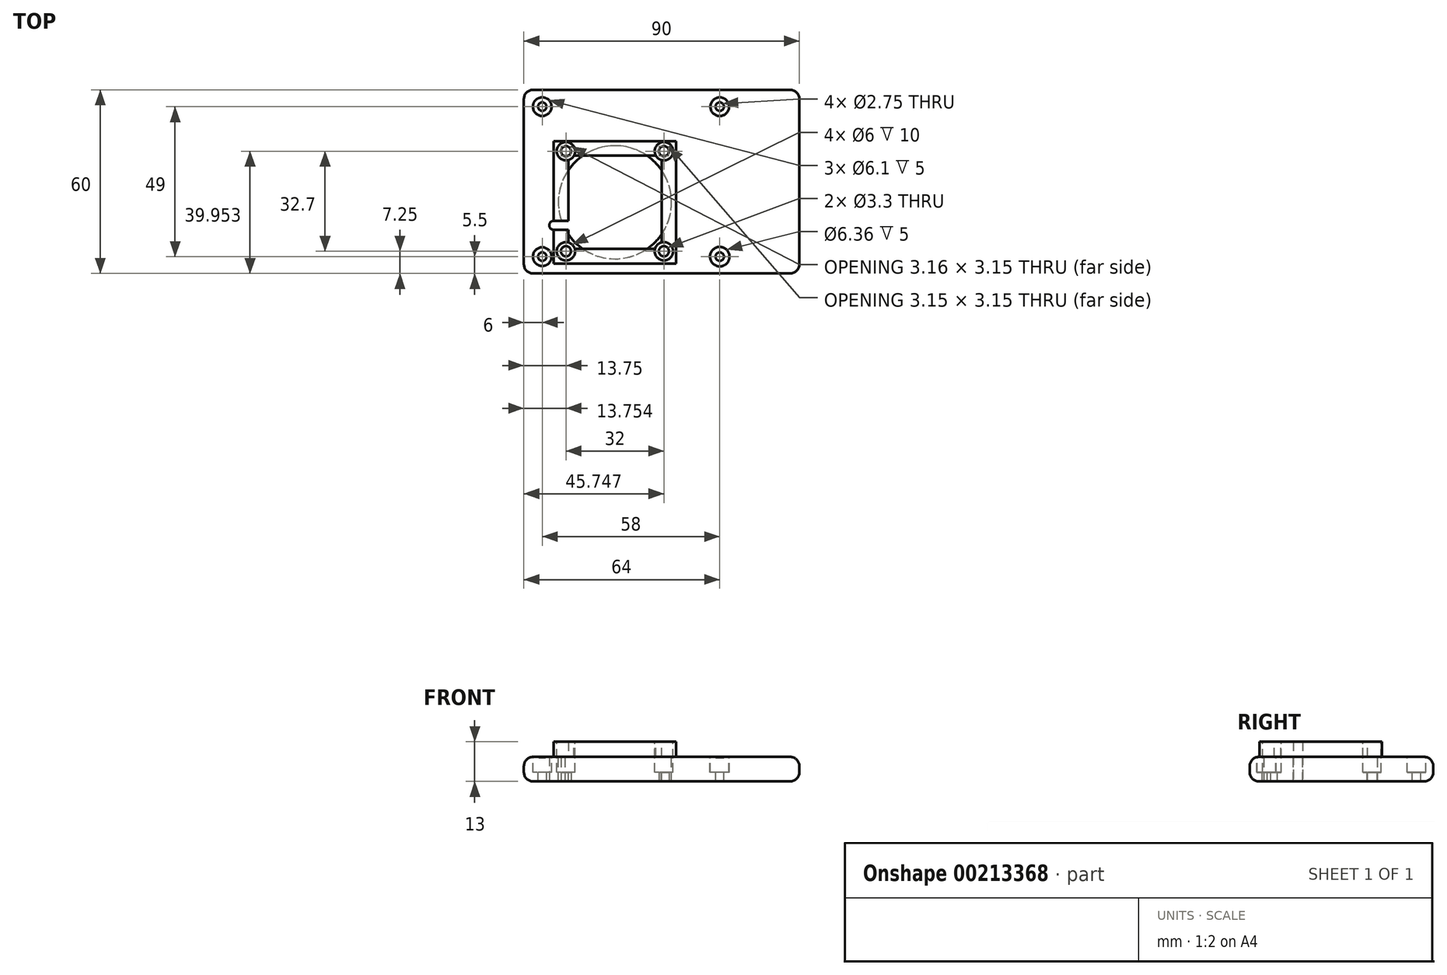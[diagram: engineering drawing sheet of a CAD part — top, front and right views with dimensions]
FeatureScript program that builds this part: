
annotation { "Feature Type Name" : "Feature", "Feature Type Description" : "" }
export const myFeature = defineFeature(function(context is Context, id is Id, definition is map)
    precondition{}
    {
        {
            var Q0;
            Q0=qCreatedBy(makeId("Top.planeOp"),FACE);
            var sketch = newSketch(context, id + "F0", { "sketchPlane" : qUnion([Q0])});
            skLineSegment(sketch, "E0.bottom", {"start": v(-45.78, -23.25) * mm, "end": v(38.22, -23.25) * mm});
            skLineSegment(sketch, "E0.top", {"start": v(-45.78, 36.75) * mm, "end": v(38.22, 36.75) * mm});
            skLineSegment(sketch, "E0.left", {"start": v(-48.78, -20.25) * mm, "end": v(-48.78, 33.75) * mm});
            skLineSegment(sketch, "E0.right", {"start": v(41.22, -20.25) * mm, "end": v(41.22, 33.75) * mm});
            skPoint(sketch, "E1.visualSharp", {"position": v(-48.78, 36.75) * mm});
            skArc(sketch, "E1.filletArc", {"start": v(-45.78, 36.75) * mm, "mid": v(-47.9, 35.87) * mm, "end": v(-48.78, 33.75) * mm});
            skPoint(sketch, "E2.visualSharp", {"position": v(41.22, 36.75) * mm});
            skArc(sketch, "E2.filletArc", {"start": v(41.22, 33.75) * mm, "mid": v(40.34, 35.87) * mm, "end": v(38.22, 36.75) * mm});
            skPoint(sketch, "E3.visualSharp", {"position": v(41.22, -23.25) * mm});
            skArc(sketch, "E3.filletArc", {"start": v(38.22, -23.25) * mm, "mid": v(40.34, -22.37) * mm, "end": v(41.22, -20.25) * mm});
            skPoint(sketch, "E4.visualSharp", {"position": v(-48.78, -23.25) * mm});
            skArc(sketch, "E4.filletArc", {"start": v(-48.78, -20.25) * mm, "mid": v(-47.9, -22.37) * mm, "end": v(-45.78, -23.25) * mm});
            skCircle(sketch, "E5", {"center": v(-42.78, -17.75) * mm, "radius": 1.38 * mm});
            skCircle(sketch, "E6", {"center": v(15.22, -17.75) * mm, "radius": 1.38 * mm});
            skCircle(sketch, "E7", {"center": v(-42.78, 31.25) * mm, "radius": 1.38 * mm});
            skCircle(sketch, "E8", {"center": v(15.22, 31.25) * mm, "radius": 1.38 * mm});
            skPoint(sketch, "E9", {"position": v(-29.78, 8.98) * mm});
            skPoint(sketch, "E10", {"position": v(2.22, -23.02) * mm});
            skLineSegment(sketch, "E11.bottom", {"start": v(-44.03, -20.25) * mm, "end": v(5.97, -20.25) * mm});
            skLineSegment(sketch, "E11.top", {"start": v(-44.03, 24.75) * mm, "end": v(5.97, 24.75) * mm});
            skLineSegment(sketch, "E11.left", {"start": v(-44.03, -20.25) * mm, "end": v(-44.03, 24.75) * mm});
            skLineSegment(sketch, "E11.right", {"start": v(5.97, -20.25) * mm, "end": v(5.97, 24.75) * mm});
            skLineSegment(sketch, "E12.bottom", {"start": v(-34.28, -15.25) * mm, "end": v(-3.78, -15.25) * mm});
            skLineSegment(sketch, "E12.top", {"start": v(-34.28, 15.25) * mm, "end": v(-3.78, 15.25) * mm});
            skLineSegment(sketch, "E12.left", {"start": v(-34.28, -15.25) * mm, "end": v(-34.28, 15.25) * mm});
            skLineSegment(sketch, "E12.right", {"start": v(-3.78, -15.25) * mm, "end": v(-3.78, 15.25) * mm});
            skCircle(sketch, "E13", {"center": v(-19.03, 0) * mm, "radius": 18.5 * mm});
            skLineSegment(sketch, "E14.bottom", {"start": v(0.97, 20) * mm, "end": v(-39.03, 20) * mm});
            skLineSegment(sketch, "E14.top", {"start": v(0.97, -20) * mm, "end": v(-39.03, -20) * mm});
            skLineSegment(sketch, "E14.left", {"start": v(0.97, 20) * mm, "end": v(0.97, -20) * mm});
            skLineSegment(sketch, "E14.right", {"start": v(-39.03, 20) * mm, "end": v(-39.03, -20) * mm});
            skCircle(sketch, "E15", {"center": v(-35.03, -16) * mm, "radius": 1.65 * mm});
            skCircle(sketch, "E16", {"center": v(-35.03, 16.7) * mm, "radius": 1.65 * mm});
            skCircle(sketch, "E17", {"center": v(-3.03, -16) * mm, "radius": 1.65 * mm});
            skCircle(sketch, "E18", {"center": v(-3.03, 16.7) * mm, "radius": 1.65 * mm});
            skCircle(sketch, "E19", {"center": v(15.22, 31.25) * mm, "radius": 3.05 * mm});
            skCircle(sketch, "E20", {"center": v(15.22, -17.75) * mm, "radius": 3.18 * mm});
            skCircle(sketch, "E21", {"center": v(-42.78, -17.75) * mm, "radius": 3.05 * mm});
            skCircle(sketch, "E22", {"center": v(-42.78, 31.25) * mm, "radius": 3.05 * mm});
            skSolve(sketch);
        }
        {
            var Q0;
            {var subQ0=sQuery(id+"F0.wireOp",EDGE,"E13");var subQ1=sQuery(id+"F0.wireOp",EDGE,"E12.bottom");var subQ2=makeQuery(id+"F0.imprint","INTERSECT",VERTEX,{"disambiguationData":[OD(0.0)],"derivedFrom":[subQ1,subQ0]});Q0=makeQuery(id+"F0.imprint","IMPRINT",FACE,{"disambiguationData":[TD([[makeQuery(id+"F0.imprint","IMPRINT",EDGE,{"disambiguationData":[TD([[subQ2,-1.0]])],"derivedFrom":subQ1}),-1.0]])]});}
            var Q1;
            {var subQ0=sQuery(id+"F0.wireOp",EDGE,"E13");var subQ1=sQuery(id+"F0.wireOp",EDGE,"E12.right");var subQ2=makeQuery(id+"F0.imprint","INTERSECT",VERTEX,{"disambiguationData":[OD(0.0)],"derivedFrom":[subQ1,subQ0]});Q1=makeQuery(id+"F0.imprint","IMPRINT",FACE,{"disambiguationData":[TD([[makeQuery(id+"F0.imprint","IMPRINT",EDGE,{"disambiguationData":[TD([[subQ2,-1.0]])],"derivedFrom":subQ1}),-1.0]])]});}
            var Q2;
            {var subQ0=sQuery(id+"F0.wireOp",EDGE,"E13");var subQ1=sQuery(id+"F0.wireOp",EDGE,"E12.top");var subQ2=makeQuery(id+"F0.imprint","INTERSECT",VERTEX,{"disambiguationData":[OD(0.0)],"derivedFrom":[subQ1,subQ0]});Q2=makeQuery(id+"F0.imprint","IMPRINT",FACE,{"disambiguationData":[TD([[makeQuery(id+"F0.imprint","IMPRINT",EDGE,{"disambiguationData":[TD([[subQ2,-1.0]])],"derivedFrom":subQ1}),1.0]])]});}
            var Q3;
            {var subQ0=sQuery(id+"F0.wireOp",EDGE,"E13");var subQ1=sQuery(id+"F0.wireOp",EDGE,"E12.left");var subQ2=makeQuery(id+"F0.imprint","INTERSECT",VERTEX,{"disambiguationData":[OD(0.0)],"derivedFrom":[subQ1,subQ0]});Q3=makeQuery(id+"F0.imprint","IMPRINT",FACE,{"disambiguationData":[TD([[makeQuery(id+"F0.imprint","IMPRINT",EDGE,{"disambiguationData":[TD([[subQ2,-1.0]])],"derivedFrom":subQ1}),1.0]])]});}
            var Q4;
            Q4=makeQuery(id+"F0.imprint","IMPRINT",FACE,{"disambiguationData":[TD([[makeQuery(id+"F0.imprint","IMPRINT",EDGE,{"derivedFrom":sQuery(id+"F0.wireOp",EDGE,"E14.bottom")}),1.0]])]});
            extrude(context, id + "F1", {"entities" : qUnion([Q0, Q1, Q2, Q3, Q4]), "depth" : 5 * mm});
        }
        {
            var Q0;
            Q0=makeQuery(id+"F0.imprint","IMPRINT",FACE,{"disambiguationData":[TD([[makeQuery(id+"F0.imprint","IMPRINT",EDGE,{"derivedFrom":sQuery(id+"F0.wireOp",EDGE,"E0.bottom")}),1.0]])]});
            var Q1;
            {var subQ6=sQuery(id+"F0.wireOp",EDGE,"E11.bottom");Q1=makeQuery(id+"F0.imprint","IMPRINT",FACE,{"disambiguationData":[TD([[makeQuery(id+"F0.imprint","IMPRINT",EDGE,{"derivedFrom":subQ6}),1.0]])]});}
            var Q2;
            {var subQ0=sQuery(id+"F0.wireOp",EDGE,"E12.right");var subQ1=sQuery(id+"F0.wireOp",EDGE,"E12.top");var subQ2=makeQuery(id+"F0.imprint","INTERSECT",VERTEX,{"derivedFrom":[subQ1,subQ0]});Q2=makeQuery(id+"F0.imprint","IMPRINT",FACE,{"disambiguationData":[TD([[makeQuery(id+"F0.imprint","IMPRINT",EDGE,{"disambiguationData":[TD([[subQ2,1.0]])],"derivedFrom":subQ1}),-1.0]])]});}
            var Q3;
            {var subQ0=sQuery(id+"F0.wireOp",EDGE,"E12.left");var subQ1=sQuery(id+"F0.wireOp",EDGE,"E12.top");var subQ2=makeQuery(id+"F0.imprint","INTERSECT",VERTEX,{"derivedFrom":[subQ1,subQ0]});Q3=makeQuery(id+"F0.imprint","IMPRINT",FACE,{"disambiguationData":[TD([[makeQuery(id+"F0.imprint","IMPRINT",EDGE,{"disambiguationData":[TD([[subQ2,-1.0]])],"derivedFrom":subQ1}),-1.0]])]});}
            var Q4;
            {var subQ0=sQuery(id+"F0.wireOp",EDGE,"E13");var subQ1=sQuery(id+"F0.wireOp",EDGE,"E12.bottom");var subQ2=makeQuery(id+"F0.imprint","INTERSECT",VERTEX,{"disambiguationData":[OD(1.0)],"derivedFrom":[subQ1,subQ0]});Q4=makeQuery(id+"F0.imprint","IMPRINT",FACE,{"disambiguationData":[TD([[makeQuery(id+"F0.imprint","IMPRINT",EDGE,{"disambiguationData":[TD([[subQ2,-1.0]])],"derivedFrom":subQ1}),1.0]])]});}
            var Q5;
            {var subQ0=sQuery(id+"F0.wireOp",EDGE,"E13");var subQ1=sQuery(id+"F0.wireOp",EDGE,"E12.top");var subQ2=makeQuery(id+"F0.imprint","INTERSECT",VERTEX,{"disambiguationData":[OD(1.0)],"derivedFrom":[subQ1,subQ0]});Q5=makeQuery(id+"F0.imprint","IMPRINT",FACE,{"disambiguationData":[TD([[makeQuery(id+"F0.imprint","IMPRINT",EDGE,{"disambiguationData":[TD([[subQ2,-1.0]])],"derivedFrom":subQ1}),-1.0]])]});}
            var Q6;
            {var subQ0=sQuery(id+"F0.wireOp",EDGE,"E16");var subQ1=sQuery(id+"F0.wireOp",EDGE,"E12.top");var subQ2=makeQuery(id+"F0.imprint","INTERSECT",VERTEX,{"derivedFrom":[subQ1,subQ0]});Q6=makeQuery(id+"F0.imprint","IMPRINT",FACE,{"disambiguationData":[TD([[makeQuery(id+"F0.imprint","IMPRINT",EDGE,{"disambiguationData":[TD([[subQ2,-1.0]])],"derivedFrom":subQ1}),-1.0]])]});}
            var Q7;
            {var subQ0=sQuery(id+"F0.wireOp",EDGE,"E15");var subQ1=sQuery(id+"F0.wireOp",EDGE,"E12.bottom");var subQ2=makeQuery(id+"F0.imprint","INTERSECT",VERTEX,{"derivedFrom":[subQ1,subQ0]});Q7=makeQuery(id+"F0.imprint","IMPRINT",FACE,{"disambiguationData":[TD([[makeQuery(id+"F0.imprint","IMPRINT",EDGE,{"disambiguationData":[TD([[subQ2,-1.0]])],"derivedFrom":subQ1}),1.0]])]});}
            var Q8;
            Q8=makeQuery(id+"F0.imprint","IMPRINT",FACE,{"disambiguationData":[TD([[makeQuery(id+"F0.imprint","IMPRINT",EDGE,{"derivedFrom":sQuery(id+"F0.wireOp",EDGE,"E14.bottom")}),1.0]])]});
            var Q9;
            Q9=makeQuery(id+"F0.imprint","IMPRINT",FACE,{"disambiguationData":[TD([[makeQuery(id+"F0.imprint","IMPRINT",EDGE,{"derivedFrom":sQuery(id+"F0.wireOp",EDGE,"E5")}),-1.0]])]});
            var Q10;
            Q10=makeQuery(id+"F0.imprint","IMPRINT",FACE,{"disambiguationData":[TD([[makeQuery(id+"F0.imprint","IMPRINT",EDGE,{"derivedFrom":sQuery(id+"F0.wireOp",EDGE,"E6")}),-1.0]])]});
            var Q11;
            Q11=makeQuery(id+"F0.imprint","IMPRINT",FACE,{"disambiguationData":[TD([[makeQuery(id+"F0.imprint","IMPRINT",EDGE,{"derivedFrom":sQuery(id+"F0.wireOp",EDGE,"E8")}),-1.0]])]});
            var Q12;
            {var subQ2=sQuery(id+"F0.wireOp",EDGE,"E11.top");Q12=makeQuery(id+"F0.imprint","IMPRINT",FACE,{"disambiguationData":[TD([[makeQuery(id+"F0.imprint","IMPRINT",EDGE,{"derivedFrom":subQ2}),-1.0]])]});}
            var Q13;
            Q13=makeQuery(id+"F0.imprint","IMPRINT",FACE,{"disambiguationData":[TD([[makeQuery(id+"F0.imprint","IMPRINT",EDGE,{"derivedFrom":sQuery(id+"F0.wireOp",EDGE,"E7")}),-1.0]])]});
            extrude(context, id + "F2", {"entities" : qUnion([Q0, Q1, Q2, Q3, Q4, Q5, Q6, Q7, Q8, Q9, Q10, Q11, Q12, Q13]), "operationType" : NewBodyOperationType.ADD, "oppositeDirection" : true, "depth" : 8 * mm});
        }
        {
            var Q0;
            Q0=makeQuery(id+"F1.opExtrude","CAP_FACE",FACE,{"disambiguationData":[OSD([sQuery(id+"F0.wireOp",EDGE,"E7"),sQuery(id+"F0.wireOp",EDGE,"E11.bottom"),sQuery(id+"F0.wireOp",EDGE,"E11.top"),sQuery(id+"F0.wireOp",EDGE,"E11.left"),sQuery(id+"F0.wireOp",EDGE,"E11.right"),sQuery(id+"F0.wireOp",EDGE,"E12.bottom"),sQuery(id+"F0.wireOp",EDGE,"E12.top"),sQuery(id+"F0.wireOp",EDGE,"E12.left"),sQuery(id+"F0.wireOp",EDGE,"E12.right"),sQuery(id+"F0.wireOp",EDGE,"E15"),sQuery(id+"F0.wireOp",EDGE,"E16"),sQuery(id+"F0.wireOp",EDGE,"E17"),sQuery(id+"F0.wireOp",EDGE,"E18")])],"isStart":false});
            var sketch = newSketch(context, id + "F3", { "sketchPlane" : qUnion([Q0])});
            skCircle(sketch, "E23", {"center": v(-35.03, 16.7) * mm, "radius": 3 * mm});
            skCircle(sketch, "E24", {"center": v(-35.03, -16) * mm, "radius": 3 * mm});
            skCircle(sketch, "E25", {"center": v(-3.03, -16) * mm, "radius": 3 * mm});
            skCircle(sketch, "E26", {"center": v(-3.03, 16.7) * mm, "radius": 3 * mm});
            skSolve(sketch);
        }
        {
            var Q0;
            {var subQ2=sQuery(id+"F0.wireOp",EDGE,"E7");var subQ4=makeQuery(id+"F1.opExtrude","CAP_EDGE",EDGE,{"disambiguationData":[OSD([subQ2])],"isStart":false});Q0=makeQuery(id+"F3.imprint","IMPRINT",FACE,{"disambiguationData":[TD([[makeQuery(id+"F3.imprint","IMPRINT",EDGE,{"derivedFrom":subQ4}),-1.0]])]});}
            var Q1;
            {var subQ5=makeQuery(id+"F1.opExtrude","CAP_EDGE",EDGE,{"disambiguationData":[OSD([sQuery(id+"F0.wireOp",EDGE,"E16")])],"isStart":false});Q1=makeQuery(id+"F3.imprint","IMPRINT",FACE,{"disambiguationData":[TD([[makeQuery(id+"F3.imprint","IMPRINT",EDGE,{"derivedFrom":subQ5}),-1.0]])]});}
            var Q2;
            {var subQ5=makeQuery(id+"F1.opExtrude","CAP_EDGE",EDGE,{"disambiguationData":[OSD([sQuery(id+"F0.wireOp",EDGE,"E15")])],"isStart":false});Q2=makeQuery(id+"F3.imprint","IMPRINT",FACE,{"disambiguationData":[TD([[makeQuery(id+"F3.imprint","IMPRINT",EDGE,{"derivedFrom":subQ5}),-1.0]])]});}
            var Q3;
            {var subQ2=sQuery(id+"F0.wireOp",EDGE,"E7");var subQ7=makeQuery(id+"F1.opExtrude","CAP_EDGE",EDGE,{"disambiguationData":[OSD([subQ2])],"isStart":false});Q3=makeQuery(id+"F3.imprint","IMPRINT",FACE,{"disambiguationData":[TD([[makeQuery(id+"F3.imprint","IMPRINT",EDGE,{"derivedFrom":subQ7}),1.0]])]});}
            var Q4;
            {var subQ5=makeQuery(id+"F1.opExtrude","CAP_EDGE",EDGE,{"disambiguationData":[OSD([sQuery(id+"F0.wireOp",EDGE,"E16")])],"isStart":false});Q4=makeQuery(id+"F3.imprint","IMPRINT",FACE,{"disambiguationData":[TD([[makeQuery(id+"F3.imprint","IMPRINT",EDGE,{"derivedFrom":subQ5}),1.0]])]});}
            var Q5;
            {var subQ5=makeQuery(id+"F1.opExtrude","CAP_EDGE",EDGE,{"disambiguationData":[OSD([sQuery(id+"F0.wireOp",EDGE,"E15")])],"isStart":false});Q5=makeQuery(id+"F3.imprint","IMPRINT",FACE,{"disambiguationData":[TD([[makeQuery(id+"F3.imprint","IMPRINT",EDGE,{"derivedFrom":subQ5}),1.0]])]});}
            var Q6;
            {var subQ5=makeQuery(id+"F1.opExtrude","CAP_EDGE",EDGE,{"disambiguationData":[OSD([sQuery(id+"F0.wireOp",EDGE,"E17")])],"isStart":false});Q6=makeQuery(id+"F3.imprint","IMPRINT",FACE,{"disambiguationData":[TD([[makeQuery(id+"F3.imprint","IMPRINT",EDGE,{"derivedFrom":subQ5}),-1.0]])]});}
            var Q7;
            {var subQ5=makeQuery(id+"F1.opExtrude","CAP_EDGE",EDGE,{"disambiguationData":[OSD([sQuery(id+"F0.wireOp",EDGE,"E17")])],"isStart":false});Q7=makeQuery(id+"F3.imprint","IMPRINT",FACE,{"disambiguationData":[TD([[makeQuery(id+"F3.imprint","IMPRINT",EDGE,{"derivedFrom":subQ5}),1.0]])]});}
            var Q8;
            {var subQ5=makeQuery(id+"F1.opExtrude","CAP_EDGE",EDGE,{"disambiguationData":[OSD([sQuery(id+"F0.wireOp",EDGE,"E18")])],"isStart":false});Q8=makeQuery(id+"F3.imprint","IMPRINT",FACE,{"disambiguationData":[TD([[makeQuery(id+"F3.imprint","IMPRINT",EDGE,{"derivedFrom":subQ5}),-1.0]])]});}
            var Q9;
            {var subQ5=makeQuery(id+"F1.opExtrude","CAP_EDGE",EDGE,{"disambiguationData":[OSD([sQuery(id+"F0.wireOp",EDGE,"E18")])],"isStart":false});Q9=makeQuery(id+"F3.imprint","IMPRINT",FACE,{"disambiguationData":[TD([[makeQuery(id+"F3.imprint","IMPRINT",EDGE,{"derivedFrom":subQ5}),1.0]])]});}
            extrude(context, id + "F4", {"entities" : qUnion([Q0, Q1, Q2, Q3, Q4, Q5, Q6, Q7, Q8, Q9]), "operationType" : NewBodyOperationType.REMOVE, "oppositeDirection" : true, "depth" : 10 * mm});
        }
        {
            var Q0;
            Q0=makeQuery(id+"F0.imprint","IMPRINT",FACE,{"disambiguationData":[TD([[makeQuery(id+"F0.imprint","IMPRINT",EDGE,{"derivedFrom":sQuery(id+"F0.wireOp",EDGE,"E5")}),-1.0]])]});
            var Q1;
            Q1=makeQuery(id+"F0.imprint","IMPRINT",FACE,{"disambiguationData":[TD([[makeQuery(id+"F0.imprint","IMPRINT",EDGE,{"derivedFrom":sQuery(id+"F0.wireOp",EDGE,"E6")}),-1.0]])]});
            var Q2;
            Q2=makeQuery(id+"F0.imprint","IMPRINT",FACE,{"disambiguationData":[TD([[makeQuery(id+"F0.imprint","IMPRINT",EDGE,{"derivedFrom":sQuery(id+"F0.wireOp",EDGE,"E8")}),-1.0]])]});
            var Q3;
            Q3=makeQuery(id+"F0.imprint","IMPRINT",FACE,{"disambiguationData":[TD([[makeQuery(id+"F0.imprint","IMPRINT",EDGE,{"derivedFrom":sQuery(id+"F0.wireOp",EDGE,"E7")}),-1.0]])]});
            extrude(context, id + "F5", {"entities" : qUnion([Q0, Q1, Q2, Q3]), "operationType" : NewBodyOperationType.REMOVE, "oppositeDirection" : true, "depth" : 5 * mm});
        }
        {
            var Q0;
            Q0=makeQuery(id+"F2.opExtrude","CAP_FACE",FACE,{"disambiguationData":[OSD([sQuery(id+"F0.wireOp",EDGE,"E0.bottom"),sQuery(id+"F0.wireOp",EDGE,"E0.top"),sQuery(id+"F0.wireOp",EDGE,"E0.left"),sQuery(id+"F0.wireOp",EDGE,"E0.right"),sQuery(id+"F0.wireOp",EDGE,"E1.filletArc"),sQuery(id+"F0.wireOp",EDGE,"E2.filletArc"),sQuery(id+"F0.wireOp",EDGE,"E3.filletArc"),sQuery(id+"F0.wireOp",EDGE,"E4.filletArc"),sQuery(id+"F0.wireOp",EDGE,"E5"),sQuery(id+"F0.wireOp",EDGE,"E6"),sQuery(id+"F0.wireOp",EDGE,"E7"),sQuery(id+"F0.wireOp",EDGE,"E8"),sQuery(id+"F0.wireOp",EDGE,"E12.top"),sQuery(id+"F0.wireOp",EDGE,"E12.left"),sQuery(id+"F0.wireOp",EDGE,"E12.right"),sQuery(id+"F0.wireOp",EDGE,"E13"),sQuery(id+"F0.wireOp",EDGE,"E15"),sQuery(id+"F0.wireOp",EDGE,"E16"),sQuery(id+"F0.wireOp",EDGE,"E17"),sQuery(id+"F0.wireOp",EDGE,"E18")])],"isStart":false});
            var sketch = newSketch(context, id + "F6", { "sketchPlane" : qUnion([Q0])});
            skCircle(sketch, "E27", {"center": v(-38.96, 7.51) * mm, "radius": 1.5 * mm});
            skLineSegment(sketch, "E28", {"start": v(-38.96, 9.01) * mm, "end": v(-34.05, 9.01) * mm});
            skLineSegment(sketch, "E29", {"start": v(-38.96, 6.01) * mm, "end": v(-34.05, 6.01) * mm});
            skLineSegment(sketch, "E30", {"start": v(-34.05, 6.01) * mm, "end": v(-34.05, 9.01) * mm});
            skSolve(sketch);
        }
        {
            var Q0;
            {var subQ0=sQuery(id+"F6.wireOp",EDGE,"E27");var subQ1=makeQuery(id+"F6.imprint","INTERSECT",VERTEX,{"derivedFrom":[subQ0,sQuery(id+"F6.wireOp",EDGE,"E28")]});Q0=makeQuery(id+"F6.imprint","IMPRINT",FACE,{"disambiguationData":[TD([[makeQuery(id+"F6.imprint","IMPRINT",EDGE,{"disambiguationData":[TD([[subQ1,-1.0]])],"derivedFrom":subQ0}),1.0]])]});}
            var Q1;
            {var subQ0=sQuery(id+"F6.wireOp",EDGE,"E28");var subQ1=sQuery(id+"F6.wireOp",EDGE,"E27");var subQ2=makeQuery(id+"F6.imprint","INTERSECT",VERTEX,{"derivedFrom":[subQ1,subQ0]});Q1=makeQuery(id+"F6.imprint","IMPRINT",FACE,{"disambiguationData":[TD([[makeQuery(id+"F6.imprint","IMPRINT",EDGE,{"disambiguationData":[TD([[subQ2,1.0]])],"derivedFrom":subQ1}),-1.0]])]});}
            var Q2;
            {var subQ0=sQuery(id+"F6.wireOp",EDGE,"E30");Q2=makeQuery(id+"F6.imprint","IMPRINT",FACE,{"disambiguationData":[TD([[makeQuery(id+"F6.imprint","IMPRINT",EDGE,{"derivedFrom":subQ0}),1.0]])]});}
            extrude(context, id + "F7", {"entities" : qUnion([Q0, Q1, Q2]), "operationType" : NewBodyOperationType.REMOVE, "endBound" : BoundingType.THROUGH_ALL, "oppositeDirection" : true, "depth" : 25 * mm});
        }
        {
            var Q0;
            Q0=makeQuery(id+"F2.opExtrude","CAP_EDGE",EDGE,{"disambiguationData":[OSD([sQuery(id+"F0.wireOp",EDGE,"E0.bottom")])],"isStart":true});
            var Q1;
            Q1=makeQuery(id+"F2.opExtrude","CAP_EDGE",EDGE,{"disambiguationData":[OSD([sQuery(id+"F0.wireOp",EDGE,"E0.bottom")])],"isStart":false});
            fillet(context, id + "F8", {"entities" : qUnion([Q0, Q1]), "radius" : 3 * mm, "tangentPropagation" : true, "allowEdgeOverflow" : false});
        }
    });
